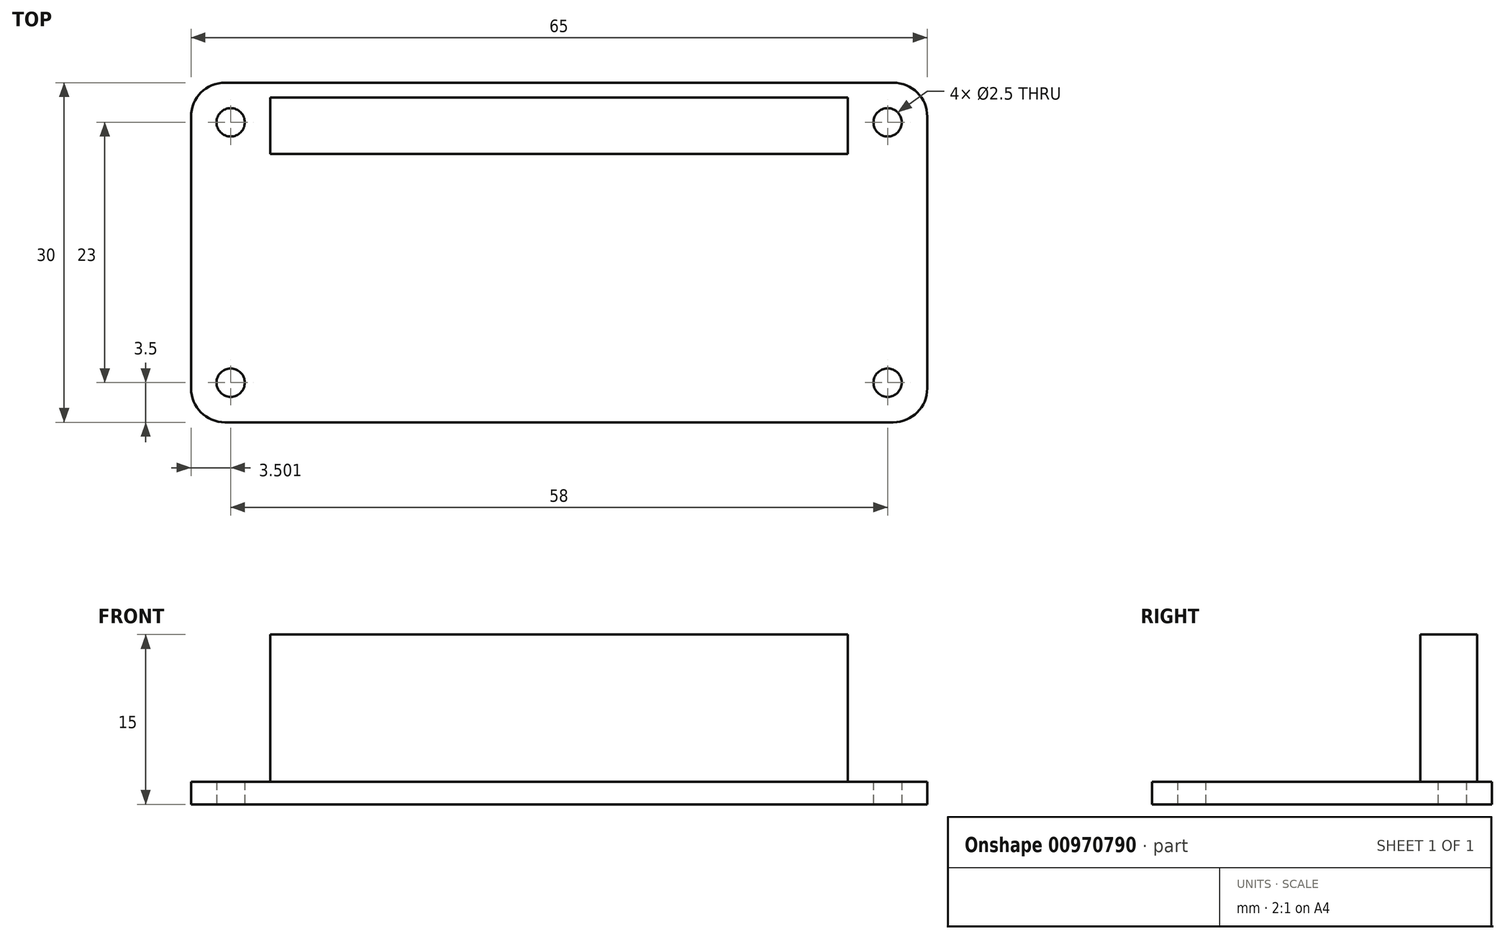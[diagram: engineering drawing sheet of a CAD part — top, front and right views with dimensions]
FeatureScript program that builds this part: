
annotation { "Feature Type Name" : "Feature", "Feature Type Description" : "" }
export const myFeature = defineFeature(function(context is Context, id is Id, definition is map)
    precondition{}
    {
        {
            var Q0;
            Q0=qCreatedBy(makeId("Top.planeOp"),FACE);
            var sketch = newSketch(context, id + "F0", { "sketchPlane" : qUnion([Q0])});
            skLineSegment(sketch, "E0.bottom", {"start": v(28.1, 15) * mm, "end": v(-30.9, 15) * mm});
            skLineSegment(sketch, "E0.top", {"start": v(28.1, -15) * mm, "end": v(-30.9, -15) * mm});
            skLineSegment(sketch, "E0.left", {"start": v(31.1, 12) * mm, "end": v(31.1, -12) * mm});
            skLineSegment(sketch, "E0.right", {"start": v(-33.9, 12) * mm, "end": v(-33.9, -12) * mm});
            skPoint(sketch, "E0.middle", {"position": v(-1.4, 0) * mm});
            skCircle(sketch, "E1", {"center": v(27.6, 11.5) * mm, "radius": 1.25 * mm});
            skPoint(sketch, "E2.visualSharp", {"position": v(31.1, 15) * mm});
            skArc(sketch, "E2.filletArc", {"start": v(31.1, 12) * mm, "mid": v(30.22, 14.12) * mm, "end": v(28.1, 15) * mm});
            skPoint(sketch, "E3.visualSharp", {"position": v(-33.9, 15) * mm});
            skArc(sketch, "E3.filletArc", {"start": v(-30.9, 15) * mm, "mid": v(-33.02, 14.12) * mm, "end": v(-33.9, 12) * mm});
            skPoint(sketch, "E4.visualSharp", {"position": v(-33.9, -15) * mm});
            skArc(sketch, "E4.filletArc", {"start": v(-33.9, -12) * mm, "mid": v(-33.02, -14.12) * mm, "end": v(-30.9, -15) * mm});
            skPoint(sketch, "E5.visualSharp", {"position": v(31.1, -15) * mm});
            skArc(sketch, "E5.filletArc", {"start": v(28.1, -15) * mm, "mid": v(30.22, -14.12) * mm, "end": v(31.1, -12) * mm});
            skCircle(sketch, "E6", {"center": v(-30.4, 11.5) * mm, "radius": 1.25 * mm});
            skCircle(sketch, "E7", {"center": v(-30.4, -11.5) * mm, "radius": 1.25 * mm});
            skCircle(sketch, "E8", {"center": v(27.6, -11.5) * mm, "radius": 1.25 * mm});
            skLineSegment(sketch, "E9.bottom", {"start": v(-26.9, 8.7) * mm, "end": v(24.1, 8.7) * mm});
            skLineSegment(sketch, "E9.top", {"start": v(-26.9, 13.7) * mm, "end": v(24.1, 13.7) * mm});
            skLineSegment(sketch, "E9.left", {"start": v(-26.9, 8.7) * mm, "end": v(-26.9, 13.7) * mm});
            skLineSegment(sketch, "E9.right", {"start": v(24.1, 8.7) * mm, "end": v(24.1, 13.7) * mm});
            skSolve(sketch);
        }
        {
            var Q0;
            Q0=makeQuery(id+"F0.imprint","IMPRINT",FACE,{"disambiguationData":[TD([[makeQuery(id+"F0.imprint","IMPRINT",EDGE,{"derivedFrom":sQuery(id+"F0.wireOp",EDGE,"E0.bottom")}),1.0]])]});
            var Q1;
            Q1=makeQuery(id+"F0.imprint","IMPRINT",FACE,{"disambiguationData":[TD([[makeQuery(id+"F0.imprint","IMPRINT",EDGE,{"derivedFrom":sQuery(id+"F0.wireOp",EDGE,"E9.bottom")}),1.0]])]});
            extrude(context, id + "F1", {"entities" : qUnion([Q0, Q1]), "depth" : 2 * mm, "offsetDistance" : 25 * mm});
        }
        {
            var Q0;
            Q0=makeQuery(id+"F0.imprint","IMPRINT",FACE,{"disambiguationData":[TD([[makeQuery(id+"F0.imprint","IMPRINT",EDGE,{"derivedFrom":sQuery(id+"F0.wireOp",EDGE,"E9.bottom")}),1.0]])]});
            extrude(context, id + "F2", {"entities" : qUnion([Q0]), "operationType" : NewBodyOperationType.ADD, "depth" : 15 * mm, "offsetDistance" : 25 * mm});
        }
    });
